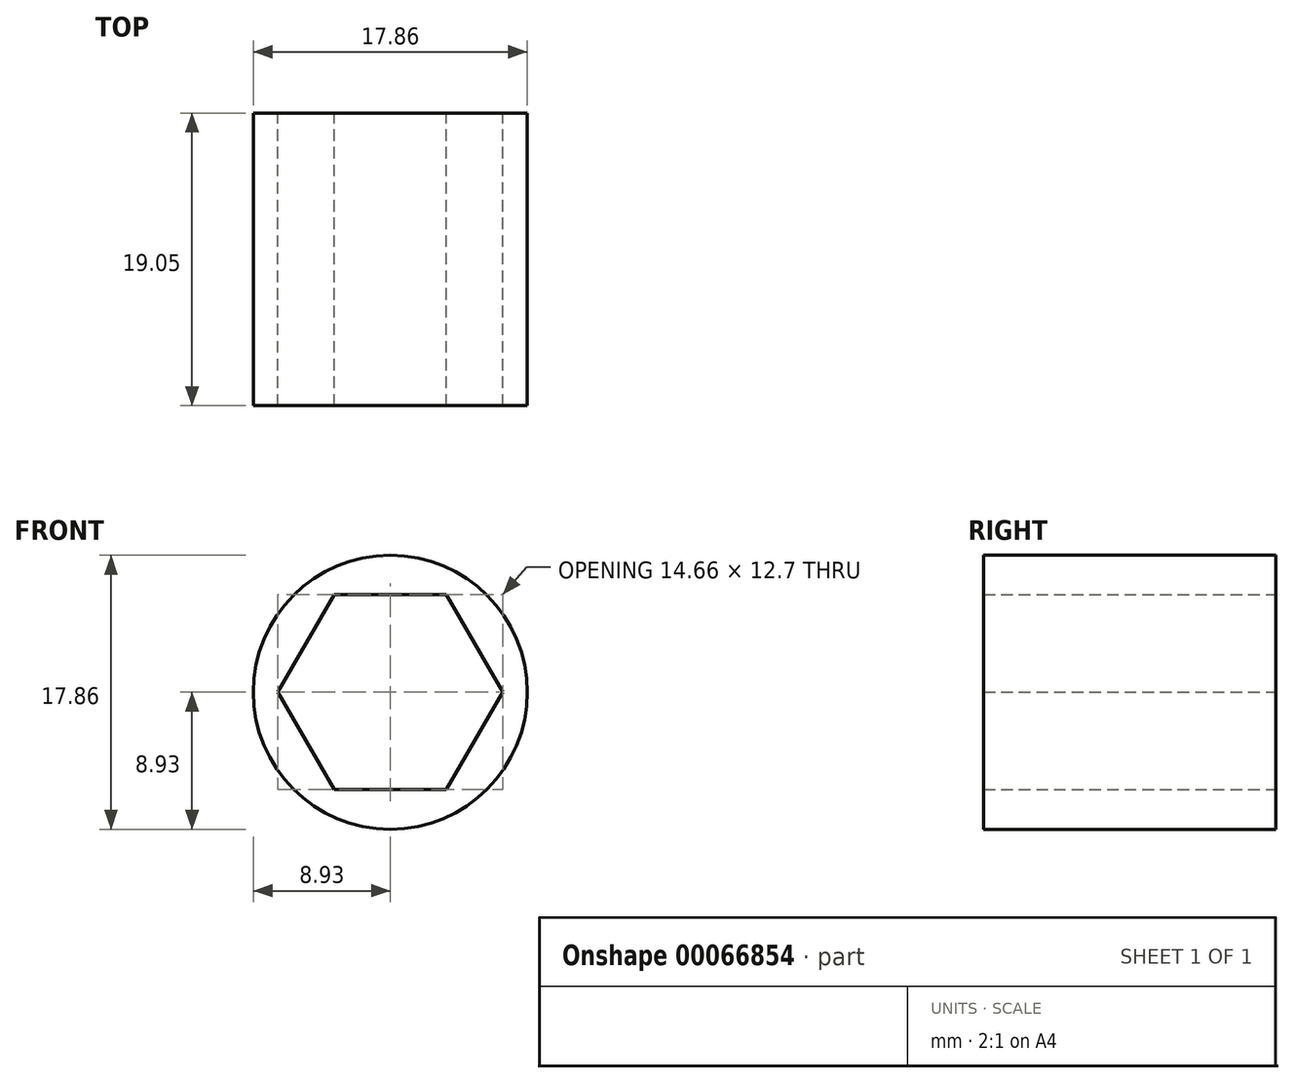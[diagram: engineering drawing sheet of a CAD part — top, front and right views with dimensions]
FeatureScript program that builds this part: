
annotation { "Feature Type Name" : "Feature", "Feature Type Description" : "" }
export const myFeature = defineFeature(function(context is Context, id is Id, definition is map)
    precondition{}
    {
        {
            var Q0;
            Q0=qCreatedBy(makeId("Front.planeOp"),FACE);
            var sketch = newSketch(context, id + "F0", { "sketchPlane" : qUnion([Q0])});
            skCircle(sketch, "E0.cCircle", {"center": v(0, 0) * mm, "radius": 6.35 * mm, "construction": true});
            skLineSegment(sketch, "E0.0", {"start": v(3.67, 6.35) * mm, "end": v(7.33, 0) * mm});
            skLineSegment(sketch, "E0.1", {"start": v(7.33, 0) * mm, "end": v(3.67, -6.35) * mm});
            skLineSegment(sketch, "E0.2", {"start": v(3.67, -6.35) * mm, "end": v(-3.67, -6.35) * mm});
            skLineSegment(sketch, "E0.3", {"start": v(-3.67, -6.35) * mm, "end": v(-7.33, 0) * mm});
            skLineSegment(sketch, "E0.4", {"start": v(-7.33, 0) * mm, "end": v(-3.67, 6.35) * mm});
            skLineSegment(sketch, "E0.5", {"start": v(-3.67, 6.35) * mm, "end": v(3.67, 6.35) * mm});
            skPoint(sketch, "E0.0.midPoint", {"position": v(5.5, 3.17) * mm});
            skCircle(sketch, "E1", {"center": v(0, 0) * mm, "radius": 8.93 * mm});
            skSolve(sketch);
        }
        {
            var Q0;
            Q0=makeQuery(id+"F0.imprint","IMPRINT",FACE,{"disambiguationData":[TD([[makeQuery(id+"F0.imprint","IMPRINT",EDGE,{"derivedFrom":sQuery(id+"F0.wireOp",EDGE,"E0.0")}),1.0]])]});
            extrude(context, id + "F1", {"entities" : qUnion([Q0]), "depth" : 19.05 * mm});
        }
    });
